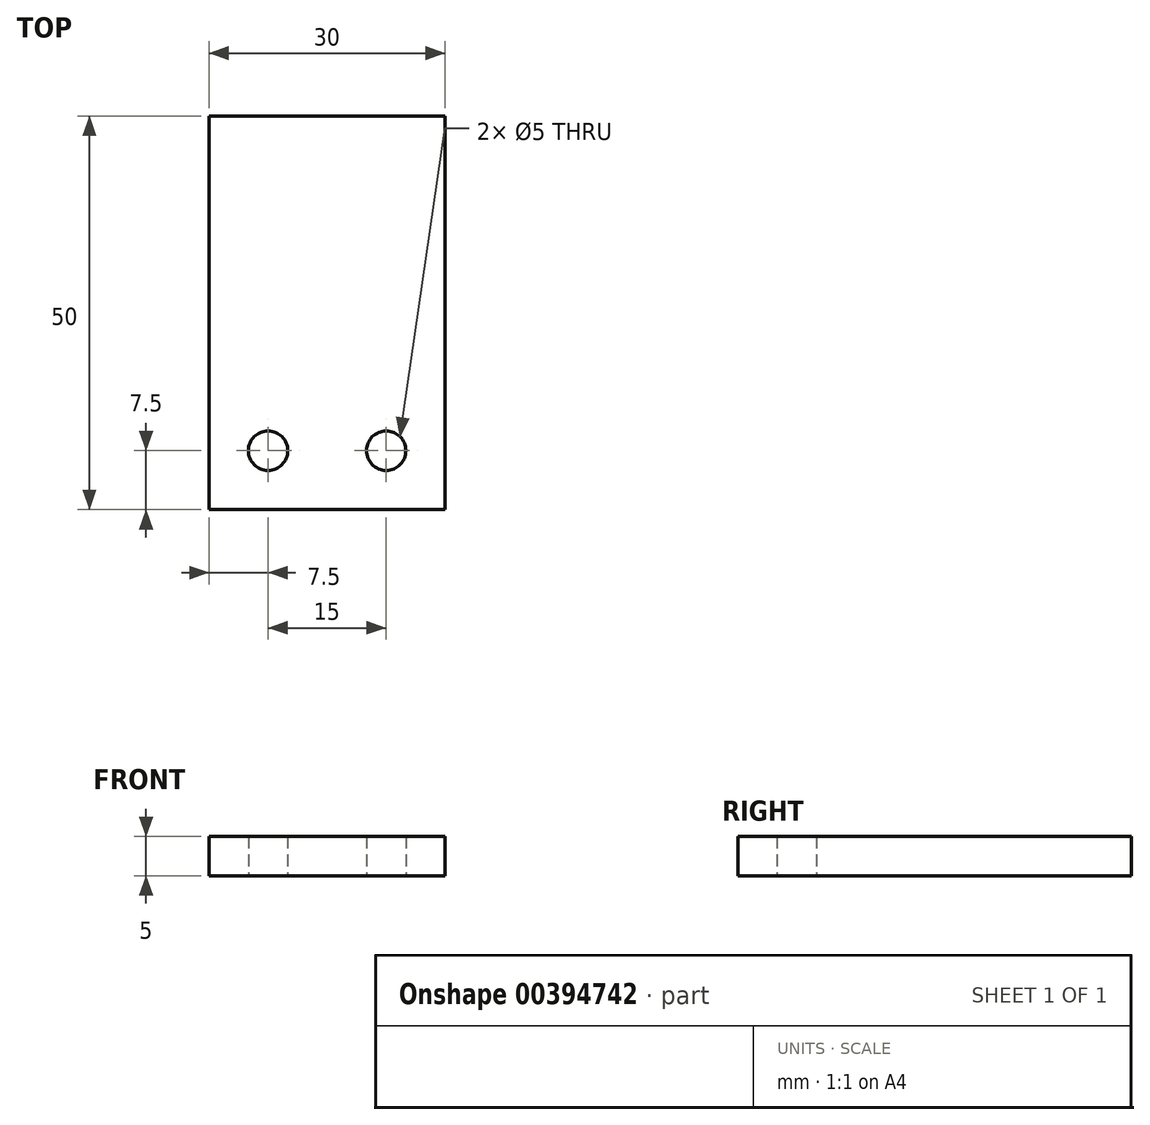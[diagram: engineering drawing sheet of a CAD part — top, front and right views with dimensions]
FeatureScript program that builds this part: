
annotation { "Feature Type Name" : "Feature", "Feature Type Description" : "" }
export const myFeature = defineFeature(function(context is Context, id is Id, definition is map)
    precondition{}
    {
        {
            var Q0;
            Q0=qCreatedBy(makeId("Top.planeOp"),FACE);
            var sketch = newSketch(context, id + "F0", { "sketchPlane" : qUnion([Q0])});
            skLineSegment(sketch, "E0.bottom", {"start": v(-15, 25) * mm, "end": v(15, 25) * mm});
            skLineSegment(sketch, "E0.top", {"start": v(-15, -25) * mm, "end": v(15, -25) * mm});
            skLineSegment(sketch, "E0.left", {"start": v(-15, 25) * mm, "end": v(-15, -25) * mm});
            skLineSegment(sketch, "E0.right", {"start": v(15, 25) * mm, "end": v(15, -25) * mm});
            skPoint(sketch, "E0.middle", {"position": v(0, 0) * mm});
            skLineSegment(sketch, "E1", {"start": v(0, 25) * mm, "end": v(0, -25) * mm, "construction": true});
            skCircle(sketch, "E2", {"center": v(-7.5, -17.5) * mm, "radius": 2.5 * mm});
            skCircle(sketch, "E3.MirrorC", {"center": v(7.5, -17.5) * mm, "radius": 2.5 * mm});
            skSolve(sketch);
        }
        {
            var Q0;
            Q0 = qSketchRegion(id + "F0", true);
            extrude(context, id + "F1", {"entities" : qUnion([Q0]), "depth" : 5 * mm});
        }
    });
